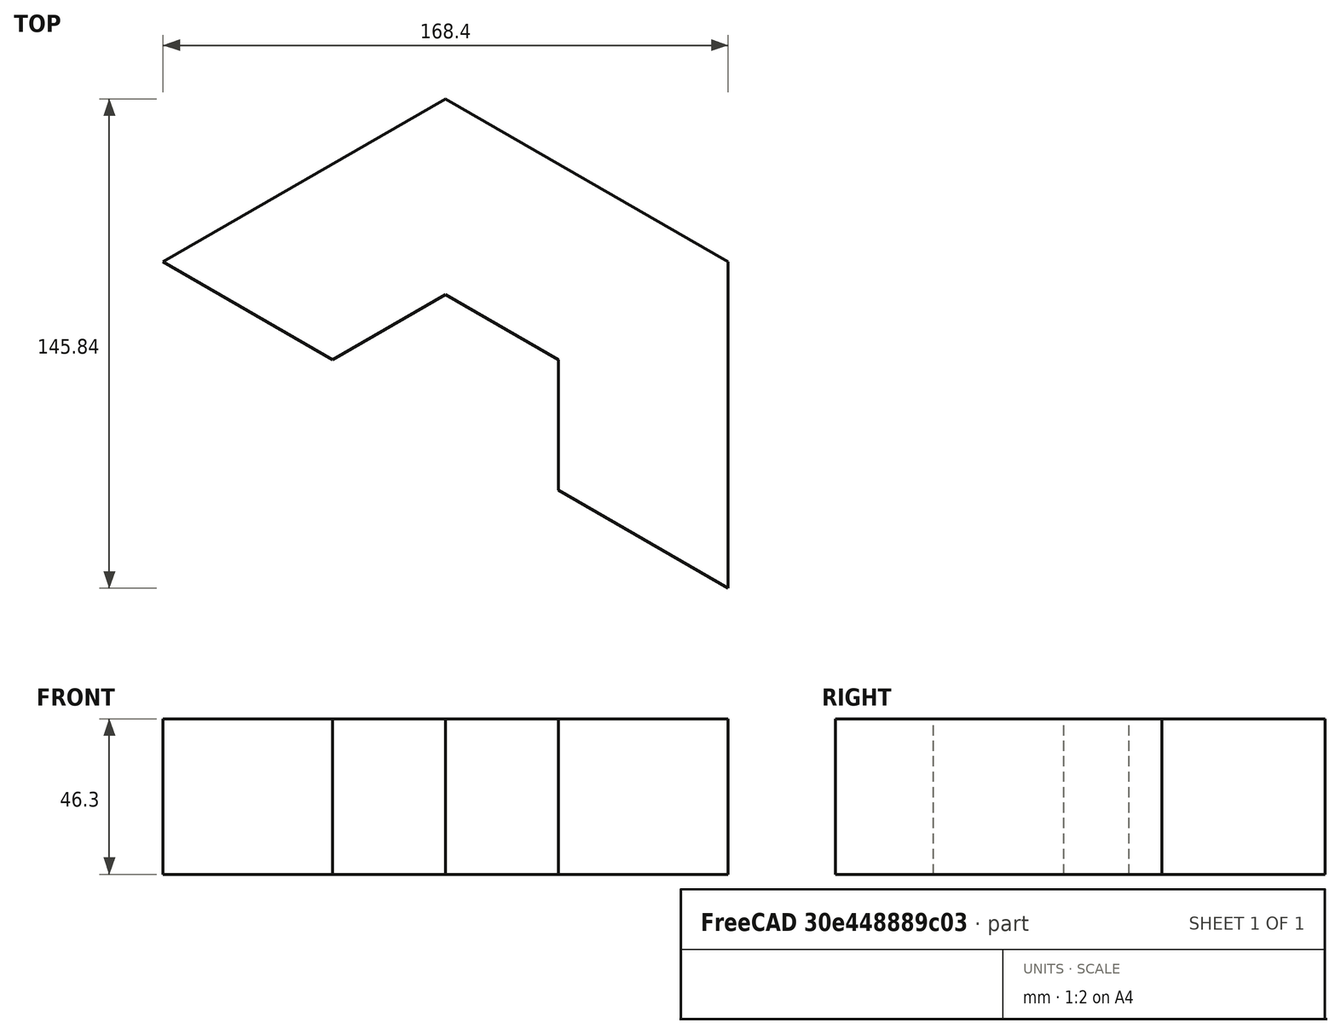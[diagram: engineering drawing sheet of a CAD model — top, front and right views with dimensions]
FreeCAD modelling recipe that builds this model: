
FCSTD DOCUMENT  (FreeCAD 0.20R29177 +426 (Git))
Label: stepperMotorStand
License: All rights reserved
LicenseURL: http://en.wikipedia.org/wiki/All_rights_reserved
objects: Sketcher::SketchObject×1, PartDesign::Pad×1, PartDesign::CoordinateSystem×1, PartDesign::Body×1
note: 5 computed .brp shape members not serialized (recipe doc carries the construction recipe); baked Part::Feature solids carry a one-line shape summary decoded from their .brp

FEATURE [Sketcher::SketchObject] Sketch
  FullyConstrained = false
  MapMode = 5
  Support = -> [XY_Plane]
  sketch-geometry (16):
    g0: LineSegment StartX=-84.2002 StartY=48.613 StartZ=0 EndX=-84.2002 EndY=-48.613 EndZ=0
    g1: LineSegment StartX=-84.2002 StartY=-48.613 StartZ=0 EndX=0 EndY=-97.226 EndZ=0
    g2: LineSegment StartX=0 StartY=-97.226 StartZ=0 EndX=84.2002 EndY=-48.613 EndZ=0
    g3: LineSegment StartX=84.2002 StartY=-48.613 StartZ=0 EndX=84.2002 EndY=48.613 EndZ=0
    g4: LineSegment StartX=84.2002 StartY=48.613 StartZ=0 EndX=0 EndY=97.226 EndZ=0
    g5: LineSegment StartX=-6e-16 StartY=97.226 StartZ=0 EndX=-84.2002 EndY=48.613 EndZ=0
    g6: Circle CenterX=0 CenterY=0 CenterZ=0 NormalX=0 NormalY=0 NormalZ=1 AngleXU=0 Radius=97.226
    g7: LineSegment StartX=-33.6434 StartY=19.424 StartZ=0 EndX=-33.6434 EndY=-19.424 EndZ=0
    g8: LineSegment StartX=-33.6434 StartY=-19.424 StartZ=0 EndX=0 EndY=-38.848 EndZ=0
    g9: LineSegment StartX=0 StartY=-38.848 StartZ=0 EndX=33.6434 EndY=-19.424 EndZ=0
    g10: LineSegment StartX=33.6434 StartY=-19.424 StartZ=0 EndX=33.6434 EndY=19.424 EndZ=0
    g11: LineSegment StartX=33.6434 StartY=19.424 StartZ=0 EndX=7.1e-15 EndY=38.848 EndZ=0
    g12: LineSegment StartX=3.8e-15 StartY=38.848 StartZ=0 EndX=-33.6434 EndY=19.424 EndZ=0
    g13: Circle CenterX=0 CenterY=0 CenterZ=0 NormalX=0 NormalY=0 NormalZ=1 AngleXU=0 Radius=38.848
    g14: LineSegment StartX=33.6434 StartY=-19.424 StartZ=0 EndX=84.2002 EndY=-48.613 EndZ=0
    g15: LineSegment StartX=-84.2002 StartY=48.613 StartZ=0 EndX=-33.6434 EndY=19.424 EndZ=0
  constraints (34):
    c: Coincident(g0,g1)
    c: Coincident(g1,g2)
    c: Coincident(g2,g3)
    c: Coincident(g3,g4)
    c: Coincident(g4,g5)
    c: Coincident(g5,g0)
    c: Equal(g0, g1-g5) x5
    c: PointOnObject(g0,g6)
    c: PointOnObject(g1,g6)
    c: PointOnObject(g2,g6)
    c: PointOnObject(g3,g6)
    c: PointOnObject(g4,g6)
    c: PointOnObject(g5,g6)
    c: Coincident(g6,g-1)
    c: Vertical(g0)
    c: Coincident(g7,g8)
    c: Coincident(g8,g9)
    c: Coincident(g9,g10)
    c: Coincident(g10,g11)
    c: Coincident(g11,g12)
    c: Coincident(g12,g7)
    c: Equal(g7, g8-g12) x5
    c: PointOnObject(g7,g13)
    c: PointOnObject(g8,g13)
    c: PointOnObject(g9,g13)
    c: PointOnObject(g10,g13)
    c: PointOnObject(g11,g13)
    c: PointOnObject(g12,g13)
    c: Vertical(g7)
    c: Coincident(g13,g6)
    c: Coincident(g14,g10)
    c: Coincident(g14,g3)
    c: Coincident(g15,g5)
    c: Coincident(g15,g12)
FEATURE [PartDesign::Pad] Pad
  Direction = (0,0,1)
  Length = 46.3
  Length2 = 10
  Profile = -> Sketch
  ReferenceAxis = -> Sketch [N_Axis]
  Type = 0
FEATURE [PartDesign::CoordinateSystem] LCS_forStepper
  AttacherType = Attacher::AttachEngine3D
  AttachmentOffset = pos=(20,0,0) rot=(0,0,1;0rad)
  MapMode = 45
  Placement = pos=(30.8456,53.4261,46.3) rot=(0,0,1;1.0472rad)
  Support = -> [Pad]
FEATURE [PartDesign::Body] Body  label="stand_Body"
  Group = -> [Sketch,Pad,LCS_forStepper]
  Origin = -> Origin
  Tip = -> Pad
